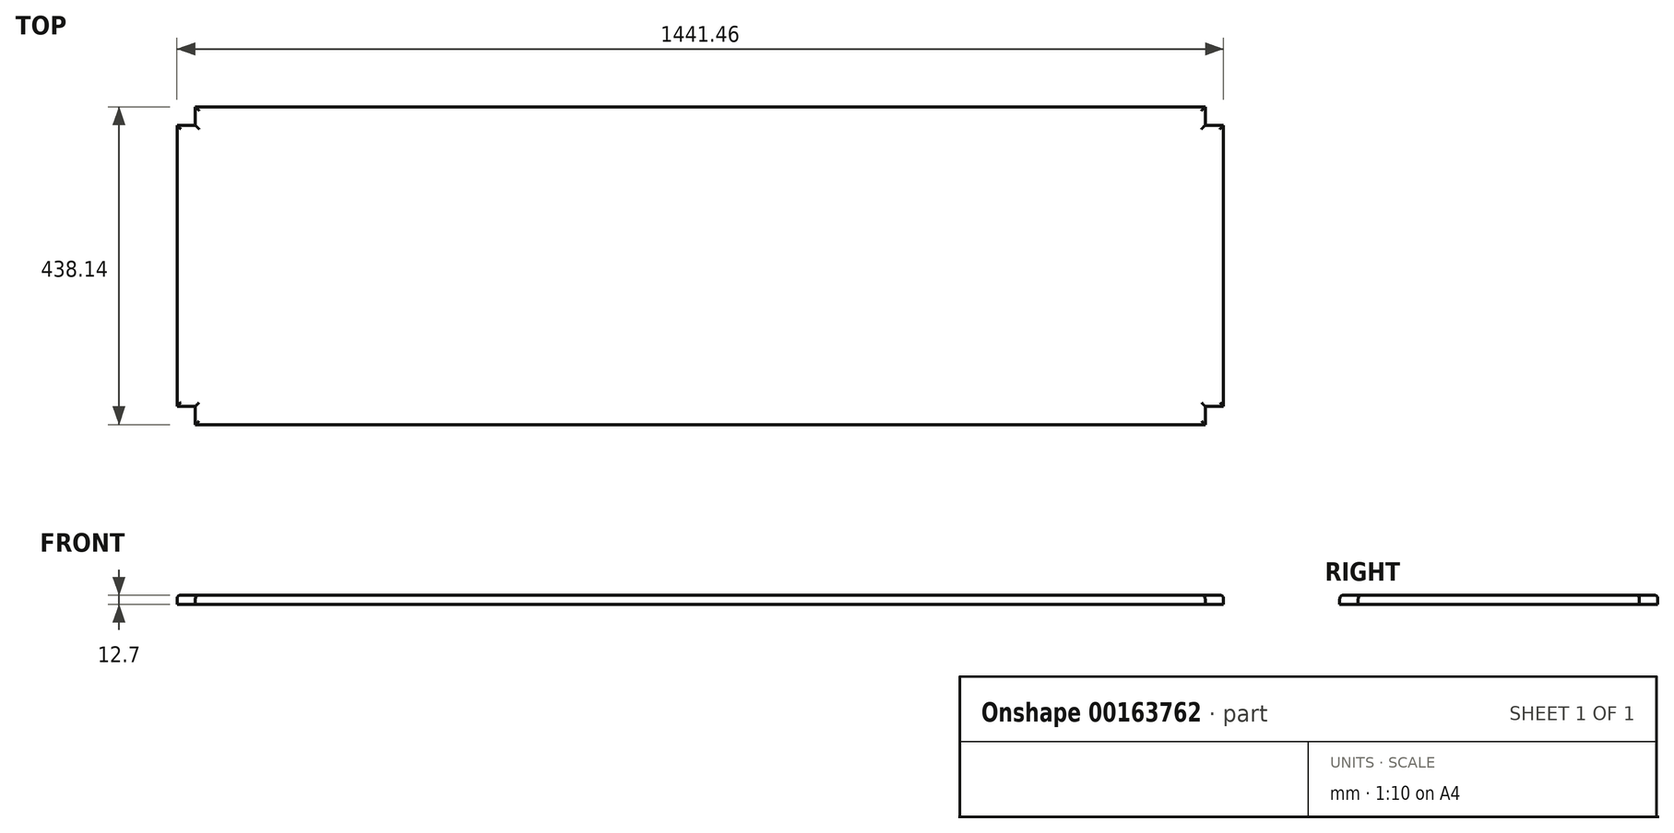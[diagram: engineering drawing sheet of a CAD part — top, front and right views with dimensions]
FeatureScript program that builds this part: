
annotation { "Feature Type Name" : "Feature", "Feature Type Description" : "" }
export const myFeature = defineFeature(function(context is Context, id is Id, definition is map)
    precondition{}
    {
        {
            var Q0;
            Q0=qCreatedBy(makeId("Top.planeOp"),FACE);
            var sketch = newSketch(context, id + "F0", { "sketchPlane" : qUnion([Q0])});
            skLineSegment(sketch, "E0.bottom", {"start": v(695.33, 219.07) * mm, "end": v(-695.33, 219.07) * mm});
            skLineSegment(sketch, "E0.top", {"start": v(695.32, -219.08) * mm, "end": v(-695.33, -219.08) * mm});
            skLineSegment(sketch, "E0.left", {"start": v(720.73, 193.68) * mm, "end": v(720.73, -193.67) * mm});
            skLineSegment(sketch, "E0.right", {"start": v(-720.73, 193.67) * mm, "end": v(-720.73, -193.68) * mm});
            skPoint(sketch, "E0.middle", {"position": v(0, 0) * mm});
            skLineSegment(sketch, "E1.top", {"start": v(-720.73, 193.67) * mm, "end": v(-695.33, 193.67) * mm});
            skLineSegment(sketch, "E1.right", {"start": v(-695.33, 219.07) * mm, "end": v(-695.33, 193.67) * mm});
            skLineSegment(sketch, "E2.top", {"start": v(-720.73, -193.68) * mm, "end": v(-695.33, -193.68) * mm});
            skLineSegment(sketch, "E2.right", {"start": v(-695.33, -219.08) * mm, "end": v(-695.33, -193.68) * mm});
            skLineSegment(sketch, "E3.top", {"start": v(720.73, 193.68) * mm, "end": v(695.33, 193.68) * mm});
            skLineSegment(sketch, "E3.right", {"start": v(695.33, 219.08) * mm, "end": v(695.33, 193.68) * mm});
            skLineSegment(sketch, "E4.top", {"start": v(720.72, -193.67) * mm, "end": v(695.32, -193.67) * mm});
            skLineSegment(sketch, "E4.right", {"start": v(695.32, -219.07) * mm, "end": v(695.32, -193.67) * mm});
            skPoint(sketch, "E5.orphan", {"position": v(-720.73, 219.07) * mm});
            skPoint(sketch, "E6.orphan", {"position": v(-720.73, -219.08) * mm});
            skPoint(sketch, "E7.orphan", {"position": v(720.73, 219.07) * mm});
            skPoint(sketch, "E8.orphan", {"position": v(720.73, -219.08) * mm});
            skSolve(sketch);
        }
        {
            var Q0;
            Q0 = qSketchRegion(id + "F0", true);
            extrude(context, id + "F1", {"entities" : qUnion([Q0]), "depth" : 12.7 * mm});
        }
        {
            var Q0;
            Q0=makeQuery(id+"F1.opExtrude","CAP_FACE",FACE,{"disambiguationData":[OSD([sQuery(id+"F0.wireOp",EDGE,"E0.bottom"),sQuery(id+"F0.wireOp",EDGE,"E0.top"),sQuery(id+"F0.wireOp",EDGE,"E0.left"),sQuery(id+"F0.wireOp",EDGE,"E0.right"),sQuery(id+"F0.wireOp",EDGE,"E1.top"),sQuery(id+"F0.wireOp",EDGE,"E1.right"),sQuery(id+"F0.wireOp",EDGE,"E2.top"),sQuery(id+"F0.wireOp",EDGE,"E2.right"),sQuery(id+"F0.wireOp",EDGE,"E3.top"),sQuery(id+"F0.wireOp",EDGE,"E3.right"),sQuery(id+"F0.wireOp",EDGE,"E4.top"),sQuery(id+"F0.wireOp",EDGE,"E4.right")])],"isStart":false});
            fillet(context, id + "F2", {"entities" : qUnion([Q0]), "radius" : 5.08 * mm, "tangentPropagation" : true, "allowEdgeOverflow" : false});
        }
    });
